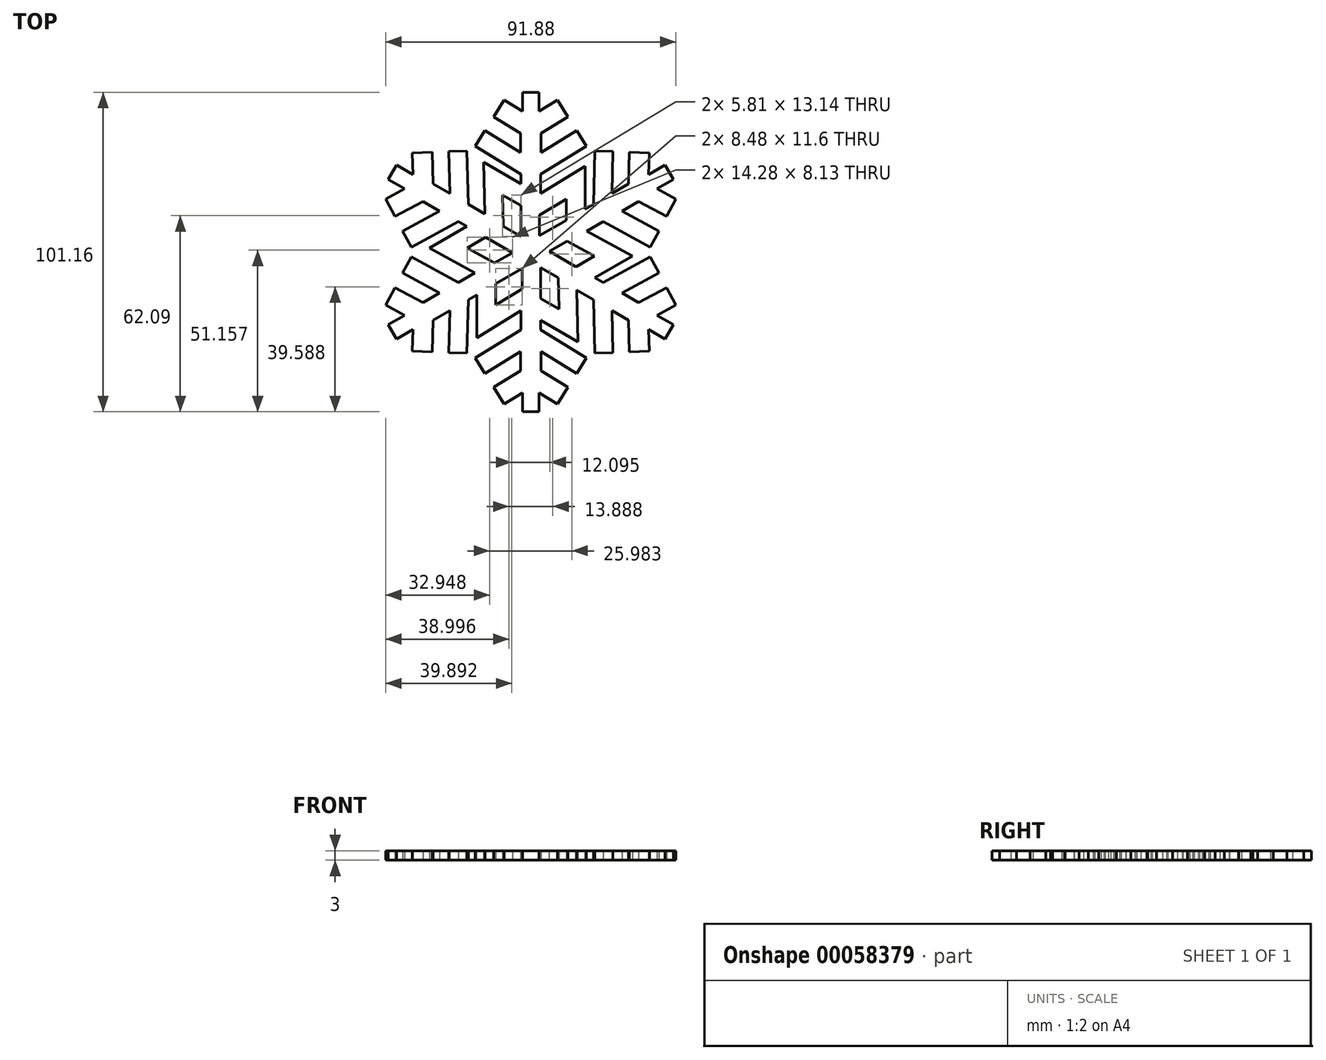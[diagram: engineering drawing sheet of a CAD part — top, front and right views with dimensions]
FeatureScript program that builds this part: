
annotation { "Feature Type Name" : "Feature", "Feature Type Description" : "" }
export const myFeature = defineFeature(function(context is Context, id is Id, definition is map)
    precondition{}
    {
        {
            var Q0;
            Q0=qCreatedBy(makeId("Top.planeOp"),FACE);
            var sketch = newSketch(context, id + "F0", { "sketchPlane" : qUnion([Q0])});
            skLineSegment(sketch, "E0", {"start": v(0, 0) * mm, "end": v(0, 50) * mm, "construction": true});
            skSolve(sketch);
        }
        {
            var Q0;
            Q0=qCreatedBy(makeId("Top.planeOp"),FACE);
            var sketch = newSketch(context, id + "F1", { "sketchPlane" : qUnion([Q0])});
            skLineSegment(sketch, "E1", {"start": v(0, 0) * mm, "end": v(-3.14, 2.47) * mm});
            skLineSegment(sketch, "E2", {"start": v(-3.14, 2.47) * mm, "end": v(-3.14, 24.67) * mm});
            skLineSegment(sketch, "E3", {"start": v(-3.14, 24.67) * mm, "end": v(-17.59, 33.5) * mm});
            skLineSegment(sketch, "E4", {"start": v(-17.59, 33.5) * mm, "end": v(-14.58, 38.43) * mm});
            skLineSegment(sketch, "E5", {"start": v(-14.58, 38.43) * mm, "end": v(-3.21, 31.48) * mm});
            skLineSegment(sketch, "E6", {"start": v(-3.21, 31.48) * mm, "end": v(-3.21, 37.56) * mm});
            skLineSegment(sketch, "E7", {"start": v(-3.21, 37.56) * mm, "end": v(-11.74, 42.82) * mm});
            skLineSegment(sketch, "E8", {"start": v(-11.74, 42.82) * mm, "end": v(-8.44, 48.17) * mm});
            skLineSegment(sketch, "E9", {"start": v(-8.44, 48.17) * mm, "end": v(-2.62, 44.59) * mm});
            skLineSegment(sketch, "E10", {"start": v(-2.62, 44.59) * mm, "end": v(-2.62, 50.58) * mm});
            skLineSegment(sketch, "E11", {"start": v(-2.62, 50.58) * mm, "end": v(0, 50.58) * mm});
            skLineSegment(sketch, "E12.MirrorCS", {"start": v(2.62, 50.58) * mm, "end": v(0, 50.58) * mm});
            skLineSegment(sketch, "E13.MirrorCS", {"start": v(2.62, 44.59) * mm, "end": v(2.62, 50.58) * mm});
            skLineSegment(sketch, "E14.MirrorCS", {"start": v(8.44, 48.17) * mm, "end": v(2.62, 44.59) * mm});
            skLineSegment(sketch, "E15.MirrorCS", {"start": v(11.74, 42.82) * mm, "end": v(8.44, 48.17) * mm});
            skLineSegment(sketch, "E16.MirrorCS", {"start": v(3.21, 37.56) * mm, "end": v(11.74, 42.82) * mm});
            skLineSegment(sketch, "E17.MirrorCS", {"start": v(3.21, 31.48) * mm, "end": v(3.21, 37.56) * mm});
            skLineSegment(sketch, "E18.MirrorCS", {"start": v(14.58, 38.43) * mm, "end": v(3.21, 31.48) * mm});
            skLineSegment(sketch, "E19.MirrorCS", {"start": v(17.59, 33.5) * mm, "end": v(14.58, 38.43) * mm});
            skLineSegment(sketch, "E20.MirrorCS", {"start": v(3.14, 24.67) * mm, "end": v(17.59, 33.5) * mm});
            skLineSegment(sketch, "E21", {"start": v(3.14, 24.67) * mm, "end": v(3.14, 18.58) * mm});
            skLineSegment(sketch, "E22", {"start": v(3.14, 18.58) * mm, "end": v(17.15, 27.18) * mm});
            skLineSegment(sketch, "E23", {"start": v(17.15, 27.18) * mm, "end": v(17.15, 9.4) * mm});
            skLineSegment(sketch, "E24", {"start": v(17.15, 9.4) * mm, "end": v(11.18, 6.12) * mm});
            skLineSegment(sketch, "E25", {"start": v(2.7, 11.66) * mm, "end": v(11.18, 16.8) * mm});
            skLineSegment(sketch, "E26", {"start": v(11.18, 16.8) * mm, "end": v(11.18, 6.12) * mm});
            skLineSegment(sketch, "E27", {"start": v(2.7, 11.66) * mm, "end": v(2.7, 1.48) * mm});
            skLineSegment(sketch, "E28.trimOffspring", {"start": v(2.7, 1.48) * mm, "end": v(0, 0) * mm});
            skSolve(sketch);
        }
        {
            var Q0;
            Q0=makeQuery(id+"F1.imprint","IMPRINT",FACE,{"disambiguationData":[TD([[makeQuery(id+"F1.imprint","IMPRINT",EDGE,{"derivedFrom":sQuery(id+"F1.wireOp",EDGE,"E1")}),-1.0]])]});
            extrude(context, id + "F2", {"entities" : qUnion([Q0]), "depth" : 3 * mm});
        }
        {
            var Q0;
            Q0=qCreatedBy(makeId("Right.planeOp"),FACE);
            var sketch = newSketch(context, id + "F3", { "sketchPlane" : qUnion([Q0])});
            skLineSegment(sketch, "E29", {"start": v(0, 0) * mm, "end": v(0, 9.85) * mm});
            skSolve(sketch);
        }
        {
            var Q0;
            Q0=makeQuery(id+"F2.opExtrude","SWEPT_BODY",BODY,{"disambiguationData":[OSD([sQuery(id+"F1.wireOp",EDGE,"E1"),sQuery(id+"F1.wireOp",EDGE,"E2"),sQuery(id+"F1.wireOp",EDGE,"E3"),sQuery(id+"F1.wireOp",EDGE,"E4"),sQuery(id+"F1.wireOp",EDGE,"E5"),sQuery(id+"F1.wireOp",EDGE,"E6"),sQuery(id+"F1.wireOp",EDGE,"E7"),sQuery(id+"F1.wireOp",EDGE,"E8"),sQuery(id+"F1.wireOp",EDGE,"E9"),sQuery(id+"F1.wireOp",EDGE,"E10"),sQuery(id+"F1.wireOp",EDGE,"E11"),sQuery(id+"F1.wireOp",EDGE,"E12.MirrorCS"),sQuery(id+"F1.wireOp",EDGE,"E13.MirrorCS"),sQuery(id+"F1.wireOp",EDGE,"E14.MirrorCS"),sQuery(id+"F1.wireOp",EDGE,"E15.MirrorCS"),sQuery(id+"F1.wireOp",EDGE,"E16.MirrorCS"),sQuery(id+"F1.wireOp",EDGE,"E17.MirrorCS"),sQuery(id+"F1.wireOp",EDGE,"E18.MirrorCS"),sQuery(id+"F1.wireOp",EDGE,"E19.MirrorCS"),sQuery(id+"F1.wireOp",EDGE,"E20.MirrorCS"),sQuery(id+"F1.wireOp",EDGE,"E21"),sQuery(id+"F1.wireOp",EDGE,"E22"),sQuery(id+"F1.wireOp",EDGE,"E23"),sQuery(id+"F1.wireOp",EDGE,"E24"),sQuery(id+"F1.wireOp",EDGE,"E25"),sQuery(id+"F1.wireOp",EDGE,"E26"),sQuery(id+"F1.wireOp",EDGE,"E27"),sQuery(id+"F1.wireOp",EDGE,"E28.trimOffspring")])]});
            var Q1;
            Q1=sQuery(id+"F3.wireOp",EDGE,"E29");
            circularPattern(context, id + "F4", {"entities" : qUnion([Q0]), "axis" : qUnion([Q1]), "angle" : 360 * degree, "instanceCount" : 6, "equalSpace" : true});
        }
        {
            var Q0;
            Q0=makeQuery(id+"F2.opExtrude","SWEPT_BODY",BODY,{"disambiguationData":[OSD([sQuery(id+"F1.wireOp",EDGE,"E1"),sQuery(id+"F1.wireOp",EDGE,"E2"),sQuery(id+"F1.wireOp",EDGE,"E3"),sQuery(id+"F1.wireOp",EDGE,"E4"),sQuery(id+"F1.wireOp",EDGE,"E5"),sQuery(id+"F1.wireOp",EDGE,"E6"),sQuery(id+"F1.wireOp",EDGE,"E7"),sQuery(id+"F1.wireOp",EDGE,"E8"),sQuery(id+"F1.wireOp",EDGE,"E9"),sQuery(id+"F1.wireOp",EDGE,"E10"),sQuery(id+"F1.wireOp",EDGE,"E11"),sQuery(id+"F1.wireOp",EDGE,"E12.MirrorCS"),sQuery(id+"F1.wireOp",EDGE,"E13.MirrorCS"),sQuery(id+"F1.wireOp",EDGE,"E14.MirrorCS"),sQuery(id+"F1.wireOp",EDGE,"E15.MirrorCS"),sQuery(id+"F1.wireOp",EDGE,"E16.MirrorCS"),sQuery(id+"F1.wireOp",EDGE,"E17.MirrorCS"),sQuery(id+"F1.wireOp",EDGE,"E18.MirrorCS"),sQuery(id+"F1.wireOp",EDGE,"E19.MirrorCS"),sQuery(id+"F1.wireOp",EDGE,"E20.MirrorCS"),sQuery(id+"F1.wireOp",EDGE,"E21"),sQuery(id+"F1.wireOp",EDGE,"E22"),sQuery(id+"F1.wireOp",EDGE,"E23"),sQuery(id+"F1.wireOp",EDGE,"E24"),sQuery(id+"F1.wireOp",EDGE,"E25"),sQuery(id+"F1.wireOp",EDGE,"E26"),sQuery(id+"F1.wireOp",EDGE,"E27"),sQuery(id+"F1.wireOp",EDGE,"E28.trimOffspring")])]});
            var Q1;
            Q1=makeQuery(id+"F4.opPattern","COPY",BODY,{"derivedFrom":makeQuery(id+"F2.opExtrude","SWEPT_BODY",BODY,{"disambiguationData":[OSD([sQuery(id+"F1.wireOp",EDGE,"E1"),sQuery(id+"F1.wireOp",EDGE,"E2"),sQuery(id+"F1.wireOp",EDGE,"E3"),sQuery(id+"F1.wireOp",EDGE,"E4"),sQuery(id+"F1.wireOp",EDGE,"E5"),sQuery(id+"F1.wireOp",EDGE,"E6"),sQuery(id+"F1.wireOp",EDGE,"E7"),sQuery(id+"F1.wireOp",EDGE,"E8"),sQuery(id+"F1.wireOp",EDGE,"E9"),sQuery(id+"F1.wireOp",EDGE,"E10"),sQuery(id+"F1.wireOp",EDGE,"E11"),sQuery(id+"F1.wireOp",EDGE,"E12.MirrorCS"),sQuery(id+"F1.wireOp",EDGE,"E13.MirrorCS"),sQuery(id+"F1.wireOp",EDGE,"E14.MirrorCS"),sQuery(id+"F1.wireOp",EDGE,"E15.MirrorCS"),sQuery(id+"F1.wireOp",EDGE,"E16.MirrorCS"),sQuery(id+"F1.wireOp",EDGE,"E17.MirrorCS"),sQuery(id+"F1.wireOp",EDGE,"E18.MirrorCS"),sQuery(id+"F1.wireOp",EDGE,"E19.MirrorCS"),sQuery(id+"F1.wireOp",EDGE,"E20.MirrorCS"),sQuery(id+"F1.wireOp",EDGE,"E21"),sQuery(id+"F1.wireOp",EDGE,"E22"),sQuery(id+"F1.wireOp",EDGE,"E23"),sQuery(id+"F1.wireOp",EDGE,"E24"),sQuery(id+"F1.wireOp",EDGE,"E25"),sQuery(id+"F1.wireOp",EDGE,"E26"),sQuery(id+"F1.wireOp",EDGE,"E27"),sQuery(id+"F1.wireOp",EDGE,"E28.trimOffspring")])]}),"instanceName":"5"});
            var Q2;
            Q2=makeQuery(id+"F4.opPattern","COPY",BODY,{"derivedFrom":makeQuery(id+"F2.opExtrude","SWEPT_BODY",BODY,{"disambiguationData":[OSD([sQuery(id+"F1.wireOp",EDGE,"E1"),sQuery(id+"F1.wireOp",EDGE,"E2"),sQuery(id+"F1.wireOp",EDGE,"E3"),sQuery(id+"F1.wireOp",EDGE,"E4"),sQuery(id+"F1.wireOp",EDGE,"E5"),sQuery(id+"F1.wireOp",EDGE,"E6"),sQuery(id+"F1.wireOp",EDGE,"E7"),sQuery(id+"F1.wireOp",EDGE,"E8"),sQuery(id+"F1.wireOp",EDGE,"E9"),sQuery(id+"F1.wireOp",EDGE,"E10"),sQuery(id+"F1.wireOp",EDGE,"E11"),sQuery(id+"F1.wireOp",EDGE,"E12.MirrorCS"),sQuery(id+"F1.wireOp",EDGE,"E13.MirrorCS"),sQuery(id+"F1.wireOp",EDGE,"E14.MirrorCS"),sQuery(id+"F1.wireOp",EDGE,"E15.MirrorCS"),sQuery(id+"F1.wireOp",EDGE,"E16.MirrorCS"),sQuery(id+"F1.wireOp",EDGE,"E17.MirrorCS"),sQuery(id+"F1.wireOp",EDGE,"E18.MirrorCS"),sQuery(id+"F1.wireOp",EDGE,"E19.MirrorCS"),sQuery(id+"F1.wireOp",EDGE,"E20.MirrorCS"),sQuery(id+"F1.wireOp",EDGE,"E21"),sQuery(id+"F1.wireOp",EDGE,"E22"),sQuery(id+"F1.wireOp",EDGE,"E23"),sQuery(id+"F1.wireOp",EDGE,"E24"),sQuery(id+"F1.wireOp",EDGE,"E25"),sQuery(id+"F1.wireOp",EDGE,"E26"),sQuery(id+"F1.wireOp",EDGE,"E27"),sQuery(id+"F1.wireOp",EDGE,"E28.trimOffspring")])]}),"instanceName":"3"});
            var Q3;
            Q3=makeQuery(id+"F4.opPattern","COPY",BODY,{"derivedFrom":makeQuery(id+"F2.opExtrude","SWEPT_BODY",BODY,{"disambiguationData":[OSD([sQuery(id+"F1.wireOp",EDGE,"E1"),sQuery(id+"F1.wireOp",EDGE,"E2"),sQuery(id+"F1.wireOp",EDGE,"E3"),sQuery(id+"F1.wireOp",EDGE,"E4"),sQuery(id+"F1.wireOp",EDGE,"E5"),sQuery(id+"F1.wireOp",EDGE,"E6"),sQuery(id+"F1.wireOp",EDGE,"E7"),sQuery(id+"F1.wireOp",EDGE,"E8"),sQuery(id+"F1.wireOp",EDGE,"E9"),sQuery(id+"F1.wireOp",EDGE,"E10"),sQuery(id+"F1.wireOp",EDGE,"E11"),sQuery(id+"F1.wireOp",EDGE,"E12.MirrorCS"),sQuery(id+"F1.wireOp",EDGE,"E13.MirrorCS"),sQuery(id+"F1.wireOp",EDGE,"E14.MirrorCS"),sQuery(id+"F1.wireOp",EDGE,"E15.MirrorCS"),sQuery(id+"F1.wireOp",EDGE,"E16.MirrorCS"),sQuery(id+"F1.wireOp",EDGE,"E17.MirrorCS"),sQuery(id+"F1.wireOp",EDGE,"E18.MirrorCS"),sQuery(id+"F1.wireOp",EDGE,"E19.MirrorCS"),sQuery(id+"F1.wireOp",EDGE,"E20.MirrorCS"),sQuery(id+"F1.wireOp",EDGE,"E21"),sQuery(id+"F1.wireOp",EDGE,"E22"),sQuery(id+"F1.wireOp",EDGE,"E23"),sQuery(id+"F1.wireOp",EDGE,"E24"),sQuery(id+"F1.wireOp",EDGE,"E25"),sQuery(id+"F1.wireOp",EDGE,"E26"),sQuery(id+"F1.wireOp",EDGE,"E27"),sQuery(id+"F1.wireOp",EDGE,"E28.trimOffspring")])]}),"instanceName":"1"});
            var Q4;
            Q4=makeQuery(id+"F4.opPattern","COPY",BODY,{"derivedFrom":makeQuery(id+"F2.opExtrude","SWEPT_BODY",BODY,{"disambiguationData":[OSD([sQuery(id+"F1.wireOp",EDGE,"E1"),sQuery(id+"F1.wireOp",EDGE,"E2"),sQuery(id+"F1.wireOp",EDGE,"E3"),sQuery(id+"F1.wireOp",EDGE,"E4"),sQuery(id+"F1.wireOp",EDGE,"E5"),sQuery(id+"F1.wireOp",EDGE,"E6"),sQuery(id+"F1.wireOp",EDGE,"E7"),sQuery(id+"F1.wireOp",EDGE,"E8"),sQuery(id+"F1.wireOp",EDGE,"E9"),sQuery(id+"F1.wireOp",EDGE,"E10"),sQuery(id+"F1.wireOp",EDGE,"E11"),sQuery(id+"F1.wireOp",EDGE,"E12.MirrorCS"),sQuery(id+"F1.wireOp",EDGE,"E13.MirrorCS"),sQuery(id+"F1.wireOp",EDGE,"E14.MirrorCS"),sQuery(id+"F1.wireOp",EDGE,"E15.MirrorCS"),sQuery(id+"F1.wireOp",EDGE,"E16.MirrorCS"),sQuery(id+"F1.wireOp",EDGE,"E17.MirrorCS"),sQuery(id+"F1.wireOp",EDGE,"E18.MirrorCS"),sQuery(id+"F1.wireOp",EDGE,"E19.MirrorCS"),sQuery(id+"F1.wireOp",EDGE,"E20.MirrorCS"),sQuery(id+"F1.wireOp",EDGE,"E21"),sQuery(id+"F1.wireOp",EDGE,"E22"),sQuery(id+"F1.wireOp",EDGE,"E23"),sQuery(id+"F1.wireOp",EDGE,"E24"),sQuery(id+"F1.wireOp",EDGE,"E25"),sQuery(id+"F1.wireOp",EDGE,"E26"),sQuery(id+"F1.wireOp",EDGE,"E27"),sQuery(id+"F1.wireOp",EDGE,"E28.trimOffspring")])]}),"instanceName":"2"});
            var Q5;
            Q5=makeQuery(id+"F4.opPattern","COPY",BODY,{"derivedFrom":makeQuery(id+"F2.opExtrude","SWEPT_BODY",BODY,{"disambiguationData":[OSD([sQuery(id+"F1.wireOp",EDGE,"E1"),sQuery(id+"F1.wireOp",EDGE,"E2"),sQuery(id+"F1.wireOp",EDGE,"E3"),sQuery(id+"F1.wireOp",EDGE,"E4"),sQuery(id+"F1.wireOp",EDGE,"E5"),sQuery(id+"F1.wireOp",EDGE,"E6"),sQuery(id+"F1.wireOp",EDGE,"E7"),sQuery(id+"F1.wireOp",EDGE,"E8"),sQuery(id+"F1.wireOp",EDGE,"E9"),sQuery(id+"F1.wireOp",EDGE,"E10"),sQuery(id+"F1.wireOp",EDGE,"E11"),sQuery(id+"F1.wireOp",EDGE,"E12.MirrorCS"),sQuery(id+"F1.wireOp",EDGE,"E13.MirrorCS"),sQuery(id+"F1.wireOp",EDGE,"E14.MirrorCS"),sQuery(id+"F1.wireOp",EDGE,"E15.MirrorCS"),sQuery(id+"F1.wireOp",EDGE,"E16.MirrorCS"),sQuery(id+"F1.wireOp",EDGE,"E17.MirrorCS"),sQuery(id+"F1.wireOp",EDGE,"E18.MirrorCS"),sQuery(id+"F1.wireOp",EDGE,"E19.MirrorCS"),sQuery(id+"F1.wireOp",EDGE,"E20.MirrorCS"),sQuery(id+"F1.wireOp",EDGE,"E21"),sQuery(id+"F1.wireOp",EDGE,"E22"),sQuery(id+"F1.wireOp",EDGE,"E23"),sQuery(id+"F1.wireOp",EDGE,"E24"),sQuery(id+"F1.wireOp",EDGE,"E25"),sQuery(id+"F1.wireOp",EDGE,"E26"),sQuery(id+"F1.wireOp",EDGE,"E27"),sQuery(id+"F1.wireOp",EDGE,"E28.trimOffspring")])]}),"instanceName":"4"});
            booleanBodies(context, id + "F5", {"operationType" : BooleanOperationType.UNION, "tools" : qUnion([Q0, Q1, Q2, Q3, Q4, Q5])});
        }
    });
